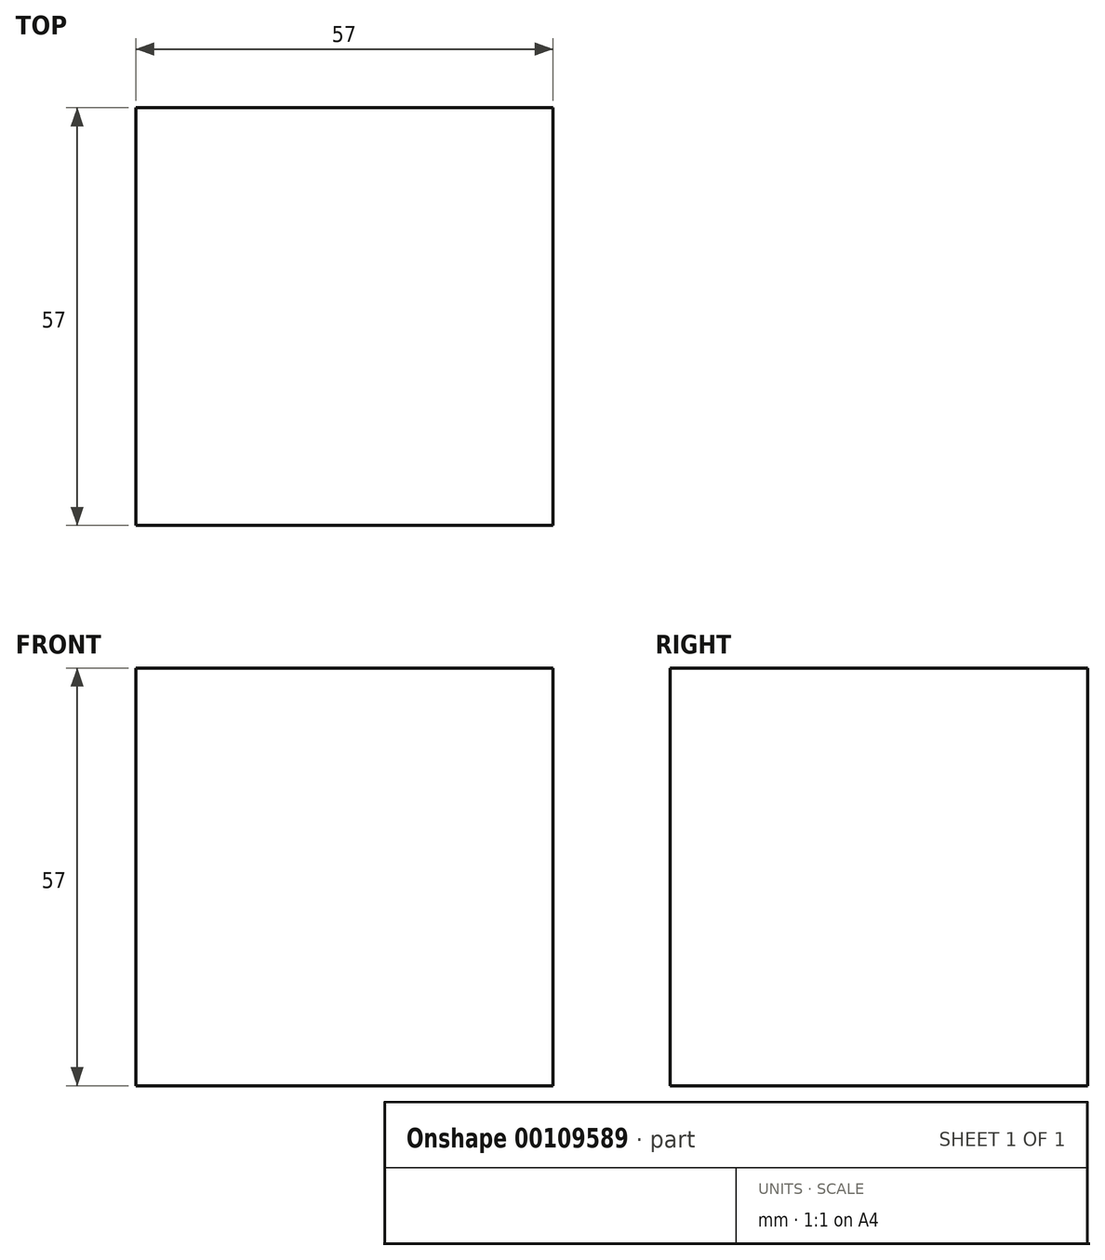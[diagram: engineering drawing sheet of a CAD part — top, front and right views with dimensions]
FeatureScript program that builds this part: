
annotation { "Feature Type Name" : "Feature", "Feature Type Description" : "" }
export const myFeature = defineFeature(function(context is Context, id is Id, definition is map)
    precondition{}
    {
        {
            var Q0;
            Q0=qCreatedBy(makeId("Top.planeOp"),FACE);
            var sketch = newSketch(context, id + "F0", { "sketchPlane" : qUnion([Q0])});
            skLineSegment(sketch, "E0.bottom", {"start": v(28.5, -28.5) * mm, "end": v(-28.5, -28.5) * mm});
            skLineSegment(sketch, "E0.top", {"start": v(28.5, 28.5) * mm, "end": v(-28.5, 28.5) * mm});
            skLineSegment(sketch, "E0.left", {"start": v(28.5, -28.5) * mm, "end": v(28.5, 28.5) * mm});
            skLineSegment(sketch, "E0.right", {"start": v(-28.5, -28.5) * mm, "end": v(-28.5, 28.5) * mm});
            skPoint(sketch, "E0.middle", {"position": v(0, 0) * mm});
            skLineSegment(sketch, "E1", {"start": v(0, 0) * mm, "end": v(0, -64.52) * mm, "construction": true});
            skLineSegment(sketch, "E2", {"start": v(0, 0) * mm, "end": v(62.98, 0) * mm, "construction": true});
            skSolve(sketch);
        }
        {
            var Q0;
            Q0=makeQuery(id+"F0.imprint","IMPRINT",FACE,{"disambiguationData":[TD([[makeQuery(id+"F0.imprint","IMPRINT",EDGE,{"derivedFrom":sQuery(id+"F0.wireOp",EDGE,"E0.bottom")}),-1.0]])]});
            extrude(context, id + "F1", {"entities" : qUnion([Q0]), "endBound" : BoundingType.SYMMETRIC, "depth" : 57 * mm});
        }
        {
            var Q0;
            Q0=qCreatedBy(makeId("Top.planeOp"),FACE);
            var Q1;
            Q1=qCreatedBy(makeId("Front.planeOp"),FACE);
            cPlane(context, id + "F2", {"entities" : qUnion([Q0, Q1]), "cplaneType" : CPlaneType.MID_PLANE, "offset" : 25 * mm, "flipAlignment" : true, "width" : 150 * mm, "height" : 150 * mm});
        }
        {
            var Q0;
            Q0=qCreatedBy(id+"F2.planeOp",FACE);
            var sketch = newSketch(context, id + "F3", { "sketchPlane" : qUnion([Q0])});
            skArc(sketch, "E3", {"start": v(37.14, 40.66) * mm, "mid": v(9.09, 29) * mm, "end": v(0, 0) * mm});
            skLineSegment(sketch, "E4", {"start": v(0, 0) * mm, "end": v(-49.57, 69.57) * mm, "construction": true});
            skSolve(sketch);
        }
        {
            var Q0;
            Q0=sQuery(id+"F3.wireOp",EDGE,"E3");
            var Q1;
            Q1=sQuery(id+"F3.wireOp",EDGE,"E4");
            revolve(context, id + "F4", {"bodyType" : ToolBodyType.SURFACE, "surfaceEntities" : qUnion([Q0]), "axis" : qUnion([Q1]), "revolveType" : RevolveType.FULL});
        }
    });
